# Revit family: RCF100-3
name_source: partatom
category: Mechanical Equipment
revit_build: Autodesk Revit 2016 (Build: 20150220_1215(x64)
units: mm (PartAtom-declared; Revit-internal decimal feet)

## family parameters
Always vertical = Yes
Cut with Voids When Loaded = No
OmniClass Number = 23.75.70.21.24.11
OmniClass Title = Constant Volume Air Terminal Units
Part Type = Normal
Room Calculation Point = No
Round Connector Dimension = Use Diameter
Shared = No
Work Plane-Based = Yes

## types (5) — shared parameters
Default Elevation = 72 "
Description = Bathroom Fan
URL = http://www.reversomatic.com

## per-type parameters (varying)
| type | CFM | Manufacturer | Model |
| RCF100-3 (Speed 1) | SP 0/CFM 64 - SP 0.10/CFM 63 - SP 0.20/CFM 64 - SP 0.30/CFM 63 - SP 0.40/CFM 64 - SP 0.50/CFM 63 - SP 0.60/CFM 63 - SP 0.70/CFM 64 - SP 0.80/CFM 64 - SP 0.90/CFM 63 - SP 1.00/CFM 63 |  | QCF-80ES |
| RCF100-3 (Speed 2) | SP 0/CFM 82 - SP 0.10/CFM 82 - SP 0.20/CFM 83 - SP 0.30/CFM 83 - SP 0.40/CFM 81 - SP 0.50/CFM 81 - SP 0.60/CFM 81 - SP 0.70/CFM 82 - SP 0.80/CFM 82 - SP 0.90/CFM 81 - SP 1.00/CFM 82 |  | QCF-80ES |
| RCF100-3 (speed 3) | SP 0/CFM 102 - SP 0.10/CFM 102 - SP 0.20/CFM 101 - SP 0.30/CFM 101 - SP 0.40/CFM 101 - SP 0.50/CFM 102 - SP 0.60/CFM 101 - SP 0.70/CFM 101 - SP 0.80/CFM 102 - SP 0.90/CFM 102 - SP 1.00/CFM 101 |  | QCF-80ES |
| RCF 100-3 (speed 4) | SP 0/CFM 120 - SP 0.10/CFM 118 - SP 0.20/CFM 118 - SP 0.30/CFM 118 - SP 0.40/CFM 120 - SP 0.50/CFM 120 - SP 0.60/CFM 120 - SP 0.70/CFM 118 - SP 0.80/CFM 118 - SP 0.90/CFM 120 - SP 1.00/CFM 120 | REVERSOMATIC | RCF100-3 |
| RCF100-3 (Speed 5) | SP 0/CFM 140 - SP 0.10/CFM 140 - SP 0.20/CFM 138 - SP 0.30/CFM 140 - SP 0.40/CFM 120 - SP 0.50/CFM 138 - SP 0.60/CFM 140 - SP 0.70/CFM 140 - SP 0.80/CFM 138- SP 0.90/CFM 140 - SP 1.00/CFM 138 |  | QCF-80ES |

## geometry (parser evidence)
native form markers: Sweep x2
no freeform markers — native parametric forms only
